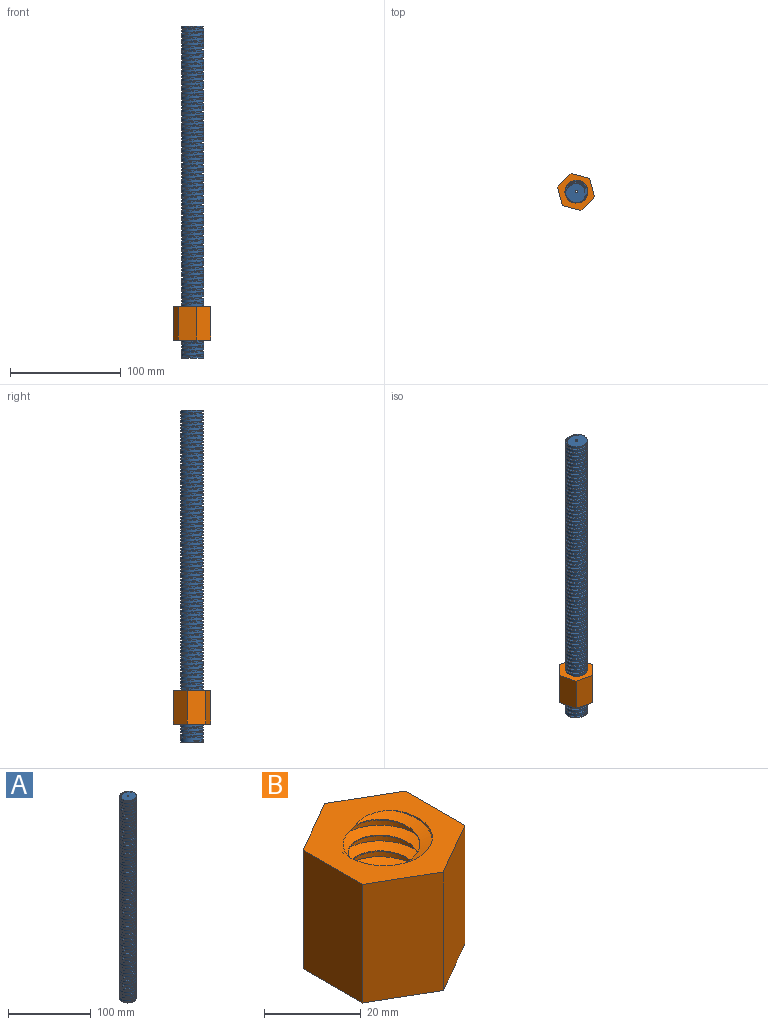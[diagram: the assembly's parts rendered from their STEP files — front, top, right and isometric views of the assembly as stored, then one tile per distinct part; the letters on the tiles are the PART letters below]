
ASSEMBLY  parts=2 mates=1
PART A: 8 faces, bbox 20x23.1x300.9 mm
  f0: cylinder r=10mm len=300mm, axis (0,0,-1), area 8878.6mm2, adj f1,f3,f4,f5,f6
  f1: plane 20x18.12mm, normal (0,0,1), area 277.3mm2, adj f0,f2,f5,f6,f7
  f2: cylinder r=1.06mm len=300mm, axis (0,0,-1), area 1993.8mm2, adj f1,f3
  f3: plane 20x20mm, normal (0,0,-1), area 310.6mm2, adj f0,f2
  f4: plane 2.6x1.6mm, normal (0,-1,0), area 2.4mm2, adj f0,f5,f6,f7
  f5: bspline ~300.7x23.09mm, area 11015.7mm2, adj f0,f1,f4,f7
  f6: bspline ~300.03x23.09mm, area 11001.9mm2, adj f0,f1,f4,f7
  f7: cylinder r=7.4mm len=299.3mm, axis (0,0,-1), area 4982.6mm2, adj f1,f4,f5,f6
PART B: 12 faces, bbox 30x34.6x32.7 mm
  f0: plane 30x17.32mm, normal (1,0,0), area 519.6mm2, adj f1,f5,f6,f7
  f1: plane 30x15mm, normal (0.5,0.87,0), area 519.6mm2, adj f0,f2,f6,f7
  f2: plane 30x15mm, normal (-0.5,0.87,0), area 519.6mm2, adj f1,f3,f6,f7
  f3: plane 30x17.32mm, normal (-1,0,0), area 519.6mm2, adj f2,f4,f6,f7
  f4: plane 30x15mm, normal (-0.5,-0.87,0), area 519.6mm2, adj f3,f5,f6,f7
  f5: plane 30x15mm, normal (0.5,-0.87,0), area 519.6mm2, adj f0,f4,f6,f7
  f6: plane 34.64x30mm, normal (0,0,1), area 498.6mm2, adj f0,f1,f2,f3,f4,f5,f8,f9
  f7: plane 34.64x30mm, normal (0,0,-1), area 498.6mm2, adj f0,f1,f2,f3,f4,f5,f8,f9
  f8: cylinder r=7.4mm len=30mm, axis (0,0,-1), area -43.8mm2, adj f6,f7,f9,f10
  f9: bspline ~32.03x23.09mm, area 1102.6mm2, adj f6,f7,f8,f11
  f10: bspline ~32.7x23.09mm, area 1111.9mm2, adj f6,f7,f8,f11
  f11: cylinder r=10mm len=30mm, axis (0,0,-1), area 1322.8mm2, adj f6,f7,f9,f10
PLACE A rot(axis=(0,0,1),7.2deg) t=(-2.84,6.58,-137.8)mm
PLACE B rot(axis=(0,0,1),75deg) t=(-3.36,6.55,-121.55)mm
MATE cylindrical A.f0 <-> B.f7  axis (0,0,-1) through (-2.84,6.58,-137.8)mm
